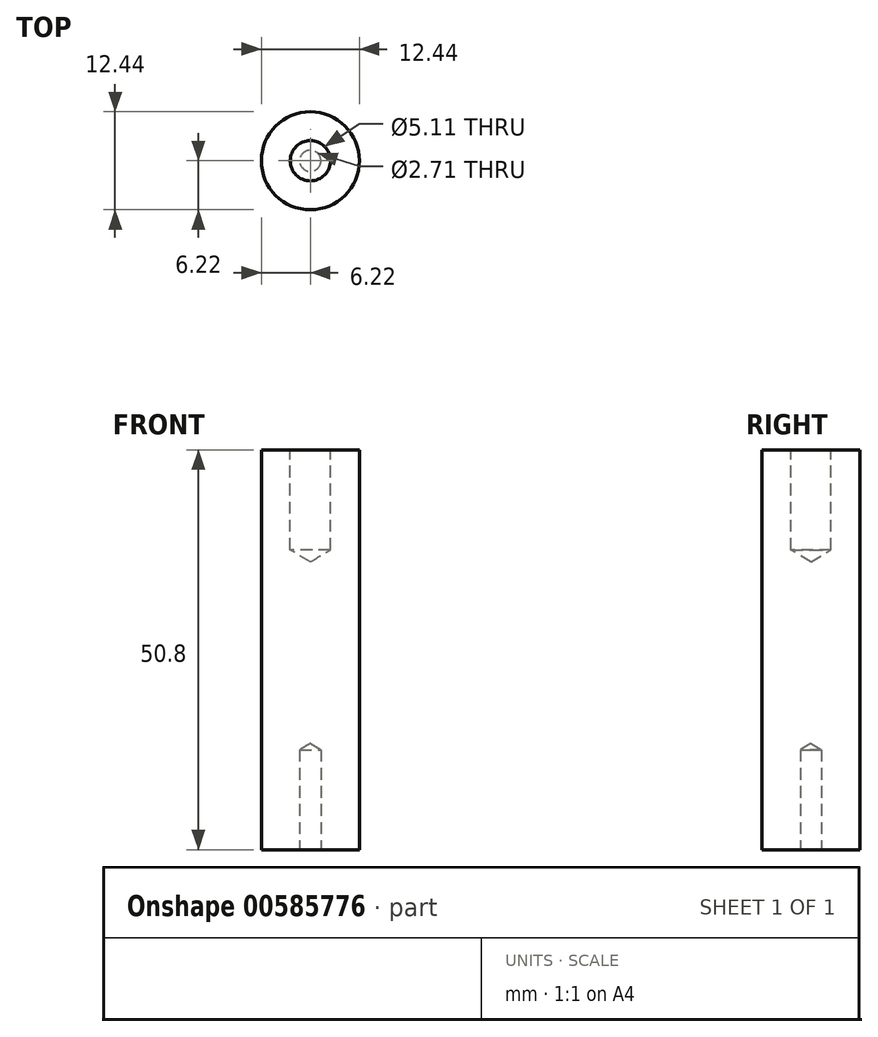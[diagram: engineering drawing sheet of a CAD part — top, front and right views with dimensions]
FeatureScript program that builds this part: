
annotation { "Feature Type Name" : "Feature", "Feature Type Description" : "" }
export const myFeature = defineFeature(function(context is Context, id is Id, definition is map)
    precondition{}
    {
        {
            var Q0;
            Q0=qCreatedBy(makeId("Top.planeOp"),FACE);
            var sketch = newSketch(context, id + "F0", { "sketchPlane" : qUnion([Q0])});
            skCircle(sketch, "E0", {"center": v(0, 0) * mm, "radius": 6.22 * mm});
            skSolve(sketch);
        }
        {
            var Q0;
            Q0=makeQuery(id+"F0.imprint","IMPRINT",FACE,{"disambiguationData":[TD([[makeQuery(id+"F0.imprint","IMPRINT",EDGE,{"derivedFrom":sQuery(id+"F0.wireOp",EDGE,"E0")}),1.0]])]});
            extrude(context, id + "F1", {"entities" : qUnion([Q0]), "oppositeDirection" : true, "depth" : 50.8 * mm});
        }
        {
            var Q0;
            Q0=makeQuery(id+"F1.opExtrude","CAP_FACE",FACE,{"disambiguationData":[OSD([sQuery(id+"F0.wireOp",EDGE,"E0")])],"isStart":true});
            var sketch = newSketch(context, id + "F2", { "sketchPlane" : qUnion([Q0])});
            skPoint(sketch, "E1", {"position": v(0, 0) * mm});
            skSolve(sketch);
        }
        {
            var Q0;
            Q0=sQuery(id+"F2.wireOp",VERTEX,"E1");
            var Q1;
            Q1=makeQuery(id+"F1.opExtrude","SWEPT_BODY",BODY,{"disambiguationData":[OSD([sQuery(id+"F0.wireOp",EDGE,"E0")])]});
            hole(context, id + "F3", {"style" : HoleStyle.SIMPLE, "endStyle" : HoleEndStyle.BLIND, "standardTappedOrClearance" : lookupTablePath({ "standard" : "ANSI", "engagement" : "75%", "pitch" : "20 tpi", "size" : "1/4", "type" : "Tapped" }), "standardBlindInLast" : lookupTablePath({ "standard" : "ANSI", "engagement" : "75%", "pitch" : "20 tpi", "size" : "1/4", "type" : "Tapped" }), "holeDiameter" : 5.1 * mm, "showTappedDepth" : true, "holeDepth" : 12.7 * mm, "isTappedThrough" : true, "tappedDepth" : 8.9 * mm, "tapClearance" : 3, "startFromSketch" : true, "locations" : qUnion([Q0]), "scope" : qUnion([Q1]), "majorDiameter" : 6.35 * mm});
        }
        {
            var Q0;
            Q0=makeQuery(id+"F1.opExtrude","CAP_FACE",FACE,{"disambiguationData":[OSD([sQuery(id+"F0.wireOp",EDGE,"E0")])],"isStart":false});
            var sketch = newSketch(context, id + "F4", { "sketchPlane" : qUnion([Q0])});
            skPoint(sketch, "E2", {"position": v(0, 0) * mm});
            skSolve(sketch);
        }
        {
            var Q0;
            Q0=sQuery(id+"F4.wireOp",VERTEX,"E2");
            var Q1;
            Q1=makeQuery(id+"F1.opExtrude","SWEPT_BODY",BODY,{"disambiguationData":[OSD([sQuery(id+"F0.wireOp",EDGE,"E0")])]});
            hole(context, id + "F5", {"style" : HoleStyle.SIMPLE, "endStyle" : HoleEndStyle.BLIND, "standardTappedOrClearance" : lookupTablePath({ "standard" : "ANSI", "engagement" : "75%", "pitch" : "32 tpi", "size" : "#6", "type" : "Tapped" }), "standardBlindInLast" : lookupTablePath({ "standard" : "ANSI", "engagement" : "75%", "pitch" : "32 tpi", "size" : "#6", "type" : "Tapped" }), "holeDiameter" : 2.7 * mm, "showTappedDepth" : true, "holeDepth" : 12.7 * mm, "isTappedThrough" : true, "tappedDepth" : 10.32 * mm, "tapClearance" : 3, "startFromSketch" : true, "locations" : qUnion([Q0]), "scope" : qUnion([Q1]), "majorDiameter" : 3.5 * mm});
        }
    });
